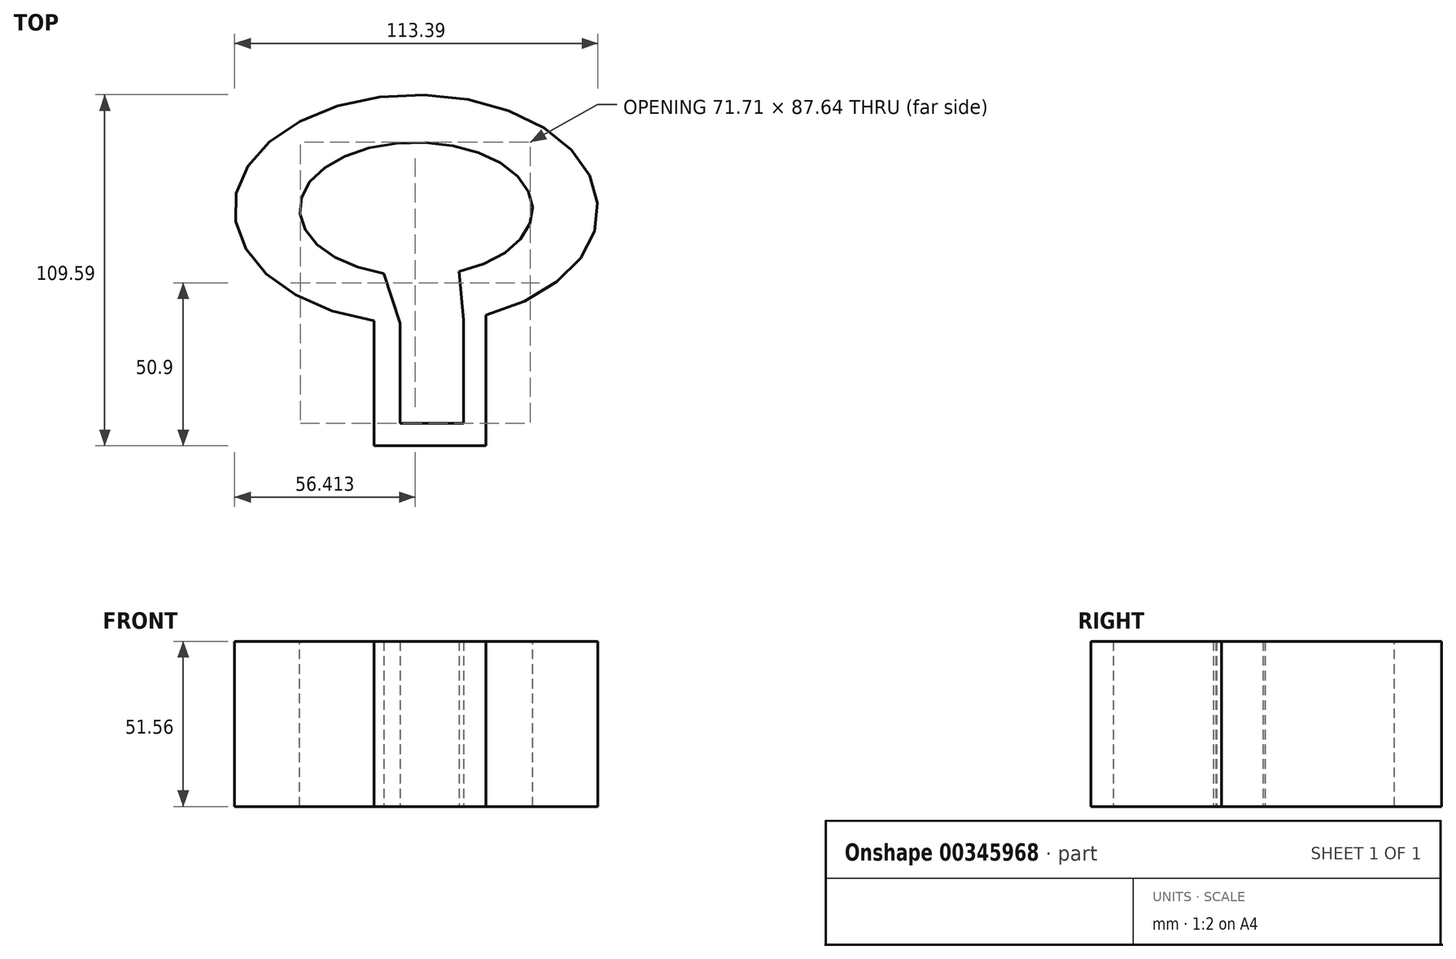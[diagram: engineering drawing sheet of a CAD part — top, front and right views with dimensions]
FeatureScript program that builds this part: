
annotation { "Feature Type Name" : "Feature", "Feature Type Description" : "" }
export const myFeature = defineFeature(function(context is Context, id is Id, definition is map)
    precondition{}
    {
        {
            var Q0;
            Q0=qCreatedBy(makeId("Top.planeOp"),FACE);
            var sketch = newSketch(context, id + "F0", { "sketchPlane" : qUnion([Q0])});
            skEllipticalArc(sketch, "E0", {});
            skLineSegment(sketch, "E1", {"start": v(-56.77, -0.49) * mm, "end": v(-56.77, -39.54) * mm});
            skLineSegment(sketch, "E2", {"start": v(-56.77, -39.54) * mm, "end": v(-21.8, -39.54) * mm});
            skLineSegment(sketch, "E3", {"start": v(-21.8, -39.54) * mm, "end": v(-21.8, 1.28) * mm});
            skEllipticalArc(sketch, "E4", {});
            skLineSegment(sketch, "E5", {"start": v(-48.62, -32.46) * mm, "end": v(-48.62, -1.33) * mm});
            skLineSegment(sketch, "E6", {"start": v(-48.62, -1.33) * mm, "end": v(-48.62, -32.46) * mm});
            skLineSegment(sketch, "E7", {"start": v(-48.62, -32.46) * mm, "end": v(-28.8, -32.46) * mm});
            skLineSegment(sketch, "E8", {"start": v(-28.8, -32.46) * mm, "end": v(-28.8, -0.23) * mm});
            skPoint(sketch, "E9.orphan", {"position": v(-43.59, 55.2) * mm});
            skPoint(sketch, "E10.orphan", {"position": v(-7.2, 34.3) * mm});
            skPoint(sketch, "E11.end.orphan", {"position": v(-79.97, 34.3) * mm});
            skPoint(sketch, "E12.end.orphan", {"position": v(-43.59, 13.38) * mm});
            skLineSegment(sketch, "E13", {"start": v(-53.68, 14.2) * mm, "end": v(-48.62, -1.33) * mm});
            skLineSegment(sketch, "E14", {"start": v(-30.24, 14.83) * mm, "end": v(-28.8, -0.23) * mm});
            const initialGuessF0  = {"E0": [-0.04358639940619469, 0.034290000796318054, 1, 0, 0.05669279955327511, 0.03575900160419565, 4.976193305053434, 4.623565019717843], "E4": [-0.04358639940619469, 0.034290000796318054, -1, 0, 0.03638413846084771, 0.020913686344677957, 1.9462507078891678, 1.2897566719420368]};
            skSetInitialGuess(sketch, initialGuessF0);
            skSolve(sketch);
        }
        {
            var Q0;
            Q0 = qSketchRegion(id + "F0", true);
            extrude(context, id + "F1", {"entities" : qUnion([Q0]), "depth" : 25.4 * mm});
        }
        {
            var Q0;
            Q0 = qSketchRegion(id + "F0", true);
            extrude(context, id + "F2", {"entities" : qUnion([Q0]), "operationType" : NewBodyOperationType.ADD, "depth" : 25.4 * mm});
        }
        {
            var Q0;
            Q0 = qSketchRegion(id + "F0", true);
            var Q1;
            Q1=makeQuery(id+"F1.opExtrude","CAP_FACE",FACE,{"disambiguationData":[OSD([sQuery(id+"F0.wireOp",EDGE,"E0"),sQuery(id+"F0.wireOp",EDGE,"E1"),sQuery(id+"F0.wireOp",EDGE,"E2"),sQuery(id+"F0.wireOp",EDGE,"E3")])],"isStart":false});
            extrude(context, id + "F3", {"entities" : qUnion([Q0, Q1]), "operationType" : NewBodyOperationType.ADD, "depth" : 25.4 * mm});
        }
        {
            var Q0;
            Q0 = qSketchRegion(id + "F0", true);
            extrude(context, id + "F4", {"entities" : qUnion([Q0]), "operationType" : NewBodyOperationType.ADD, "depth" : 25.4 * mm});
        }
        {
            var Q0;
            Q0 = qSketchRegion(id + "F0", true);
            extrude(context, id + "F5", {"entities" : qUnion([Q0]), "operationType" : NewBodyOperationType.ADD, "oppositeDirection" : true, "depth" : 0.5 * mm});
        }
        {
            var Q0;
            Q0 = qSketchRegion(id + "F0", true);
            extrude(context, id + "F6", {"entities" : qUnion([Q0]), "operationType" : NewBodyOperationType.ADD, "depth" : 0.5 * mm});
        }
        {
            var Q0;
            Q0 = qSketchRegion(id + "F0", true);
            extrude(context, id + "F7", {"entities" : qUnion([Q0]), "operationType" : NewBodyOperationType.ADD, "oppositeDirection" : true, "depth" : 0.76 * mm});
        }
    });
